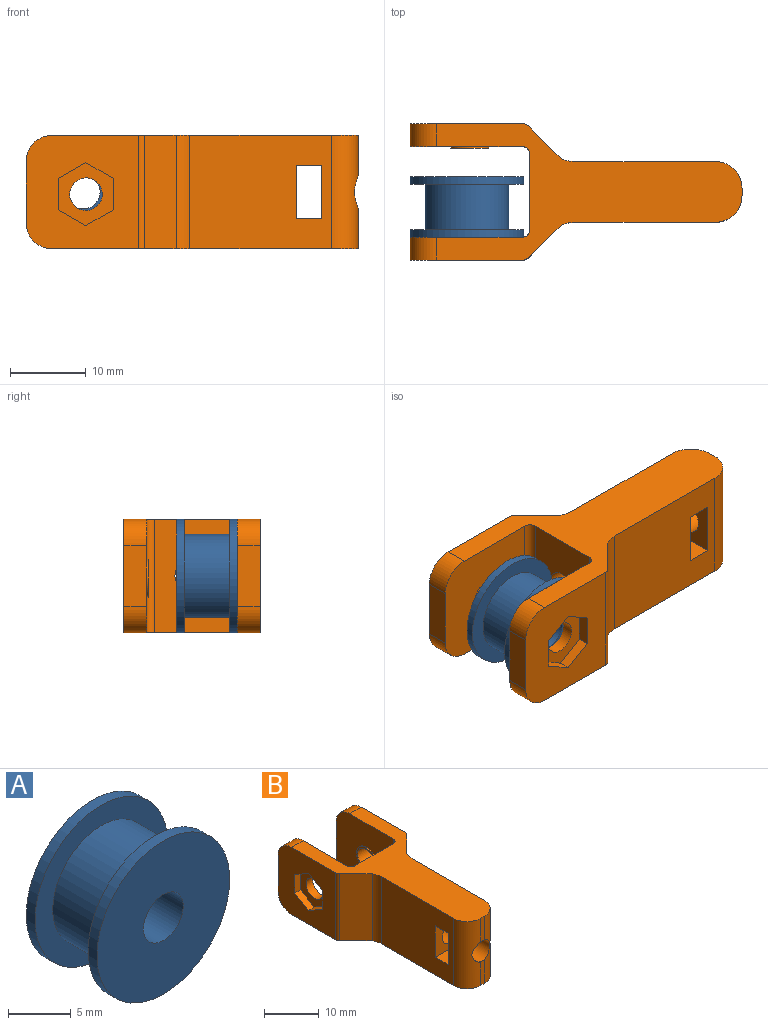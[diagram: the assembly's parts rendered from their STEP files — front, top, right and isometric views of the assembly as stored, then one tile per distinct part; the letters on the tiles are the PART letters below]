
ASSEMBLY  parts=2 mates=1
PART A: 8 faces, bbox 15x8x15 mm
  f0: cylinder r=2.25mm len=8mm, axis (0,-1,0), area 113.1mm2, adj f2,f6
  f1: cylinder r=7.5mm len=15mm, axis (0,-1,0), area 47.1mm2, adj f2,f3
  f2: plane 15x15mm, normal (0,1,0), area 160.8mm2, adj f0,f1
  f3: plane 15x15mm, normal (0,-1,0), area 81.7mm2, adj f1,f4
  f4: cylinder r=5.5mm len=11mm, axis (0,1,0), area 207.3mm2, adj f3,f7
  f5: cylinder r=7.5mm len=15mm, axis (0,1,0), area 47.1mm2, adj f6,f7
  f6: plane 15x15mm, normal (0,-1,0), area 160.8mm2, adj f0,f5
  f7: plane 15x15mm, normal (0,1,0), area 81.7mm2, adj f4,f5
PART B: 46 faces, bbox 18x43.8x15 mm
  f0: plane 5.31x1mm, normal (0,-1,0), area 5.3mm2, adj f4,f12,f32,f33
  f1: plane 15x14.89mm, normal (-1,0,0), area 173.1mm2, adj f10,f12,f13,f21,f22,f23,f24,f25
  f2: plane 18.7x15mm, normal (1,0,0), area 257.4mm2, adj f12,f13,f17,f18,f19,f20,f30,f33
  f3: plane 18.7x15mm, normal (-1,0,0), area 257.4mm2, adj f12,f13,f17,f18,f19,f20,f31,f32
  f4: cylinder r=2.25mm len=4.85mm, axis (0,-1,0), area 65.7mm2, adj f0,f11,f19,f32,f33
  f5: plane 15x14.89mm, normal (1,0,0), area 203.5mm2, adj f6,f12,f13,f16,f34,f36,f39
  f6: plane 8x3mm, normal (0,1,0), area 24mm2, adj f5,f7,f34,f36
  f7: plane 15x14.8mm, normal (-1,0,0), area 197.1mm2, adj f6,f12,f13,f34,f36,f40,f42
  f8: plane 15x10mm, normal (0,1,0), area 134.1mm2, adj f12,f13,f14,f40,f41
  f9: plane 15x14.8mm, normal (1,0,0), area 197.1mm2, adj f10,f12,f13,f35,f37,f41,f44
  f10: plane 8x3mm, normal (0,1,0), area 24mm2, adj f1,f9,f35,f37
  f11: plane 5.31x1mm, normal (0,-1,0), area 5.3mm2, adj f4,f13,f32,f33
  f12: plane 40.3x18mm, normal (0,0,1), area 313.3mm2, adj f0,f1,f2,f3,f5,f7,f8,f9
  f13: plane 40.3x18mm, normal (0,0,-1), area 313.3mm2, adj f1,f2,f3,f5,f7,f8,f9,f11
  f14: cylinder r=2.25mm len=19.85mm, axis (0,-1,0), area 280.6mm2, adj f8,f20
  f15: cylinder r=2.15mm len=4.3mm, axis (-1,0,0), area 23mm2, adj f27,f45
  f16: cylinder r=2.15mm len=4.3mm, axis (-1,0,0), area 43.2mm2, adj f5,f43
  f17: plane 8x3.3mm, normal (0,0,1), area 26.4mm2, adj f2,f3,f19,f20
  f18: plane 8x3.3mm, normal (0,0,-1), area 26.4mm2, adj f2,f3,f19,f20
  f19: plane 8x7mm, normal (0,1,0), area 40.1mm2, adj f2,f3,f4,f17,f18
  f20: plane 8x7mm, normal (0,-1,0), area 40.1mm2, adj f2,f3,f14,f17,f18
  f21: plane 3.6x2.08mm, normal (0,0.5,-0.87), area 6.2mm2, adj f1,f22,f26,f27
  f22: plane 3.6x2.08mm, normal (0,-0.5,-0.87), area 6.2mm2, adj f1,f21,f23,f27
  f23: plane 4.16x1.5mm, normal (0,-1,0), area 6.2mm2, adj f1,f22,f24,f27
  f24: plane 3.6x2.08mm, normal (0,-0.5,0.87), area 6.2mm2, adj f1,f23,f25,f27
  f25: plane 3.6x2.08mm, normal (0,0.5,0.87), area 6.2mm2, adj f1,f24,f26,f27
  f26: plane 4.16x1.5mm, normal (0,1,0), area 6.2mm2, adj f1,f21,f25,f27
  f27: plane 8.31x7.2mm, normal (-1,0,0), area 30.4mm2, adj f15,f21,f22,f23,f24,f25,f26
  f28: plane 15x4.21mm, normal (0.71,-0.71,0), area 89.2mm2, adj f12,f13,f30,f39
  f29: plane 15x4.21mm, normal (-0.71,-0.71,0), area 89.2mm2, adj f12,f13,f31,f38
  f30: cylinder r=3.5mm len=15mm, axis (0,0,-1), area 28.4mm2, adj f2,f12,f13,f28
  f31: cylinder r=3.5mm len=15mm, axis (0,0,1), area 28.4mm2, adj f3,f12,f13,f29
  f32: cylinder r=3.5mm len=15mm, axis (0,0,-1), area 76.6mm2, adj f0,f3,f4,f11,f12,f13
  f33: cylinder r=3.5mm len=15mm, axis (0,0,-1), area 76.6mm2, adj f0,f2,f4,f11,f12,f13
  f34: cylinder r=3.5mm len=3.5mm, axis (-1,0,0), area 16.5mm2, adj f5,f6,f7,f13
  f35: cylinder r=3.5mm len=3.5mm, axis (-1,0,0), area 16.5mm2, adj f1,f9,f10,f13
  f36: cylinder r=3.5mm len=3.5mm, axis (1,0,0), area 16.5mm2, adj f5,f6,f7,f12
  f37: cylinder r=3.5mm len=3.5mm, axis (1,0,0), area 16.5mm2, adj f1,f9,f10,f12
  f38: cylinder r=1mm len=15mm, axis (0,0,-1), area 11.8mm2, adj f1,f12,f13,f29
  f39: cylinder r=1mm len=15mm, axis (0,0,1), area 11.8mm2, adj f5,f12,f13,f28
  f40: cylinder r=1mm len=15mm, axis (0,0,1), area 23.6mm2, adj f7,f8,f12,f13
  f41: cylinder r=1mm len=15mm, axis (0,0,1), area 23.6mm2, adj f8,f9,f12,f13
  f42: cylinder r=2.5mm len=5mm, axis (1,0,0), area 3.1mm2, adj f7,f43
  f43: plane 5x5mm, normal (-1,0,0), area 5.1mm2, adj f16,f42
  f44: cylinder r=2.5mm len=5mm, axis (-1,0,0), area 3.1mm2, adj f9,f45
  f45: plane 5x5mm, normal (1,0,0), area 5.1mm2, adj f15,f44
PLACE A rot(axis=(0,0,-1),0deg) t=(-11.26,-8.02,1.06)mm
PLACE B rot(axis=(0,0,1),90deg) t=(-2.98,-15.02,-6.47)mm
MATE revolute A.f0 <-> B.f9  axis (0,-1,0) through (-11.26,-15.02,1.06)mm
